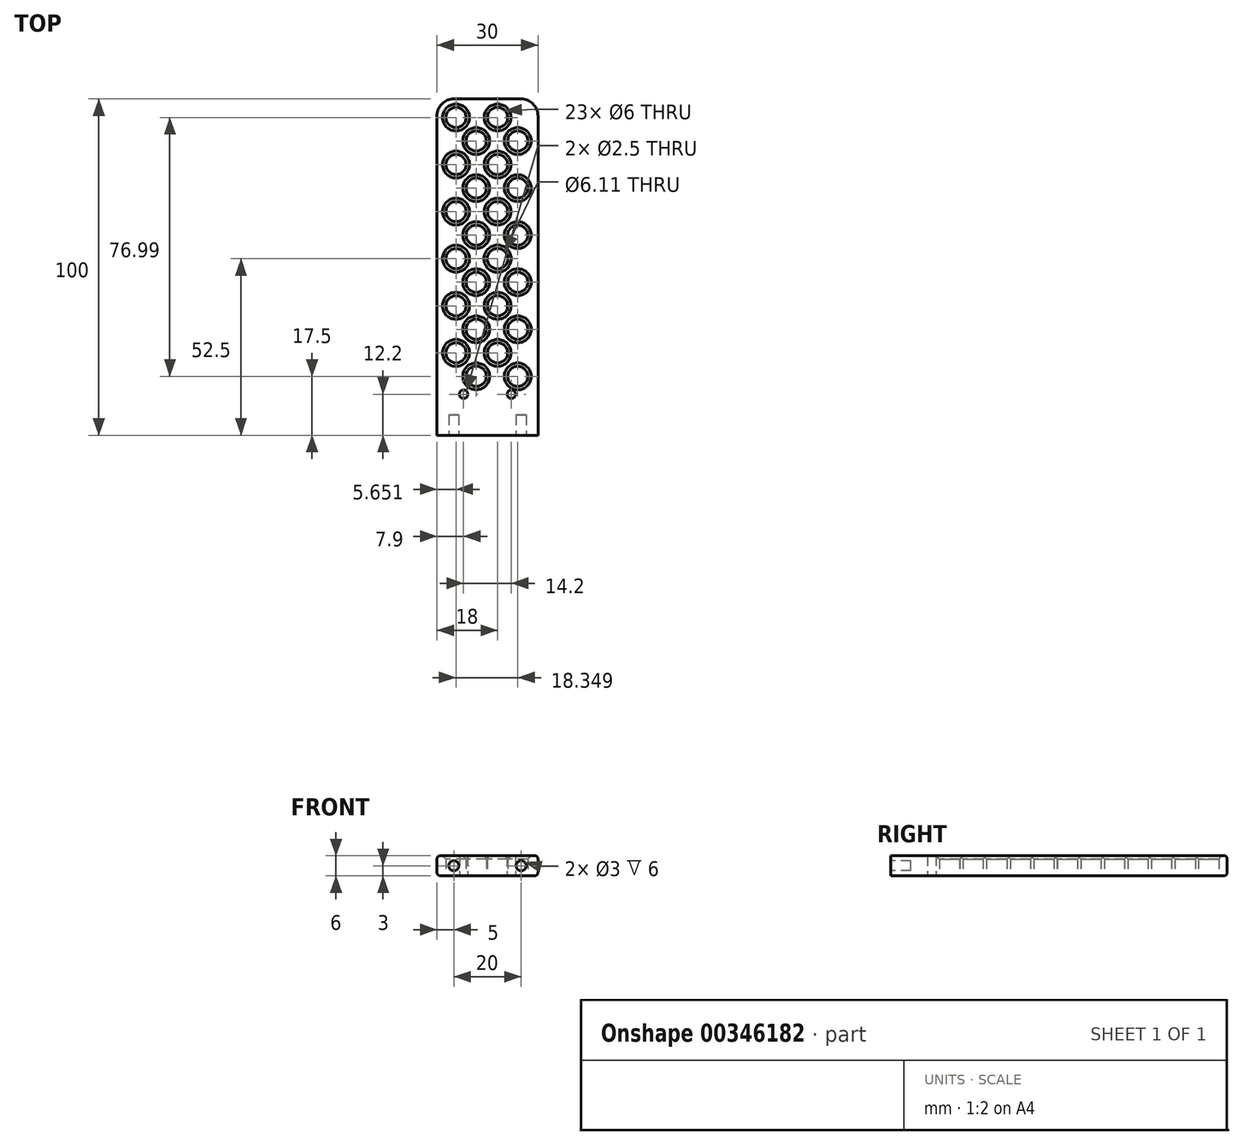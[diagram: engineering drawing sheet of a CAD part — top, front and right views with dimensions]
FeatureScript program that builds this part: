
annotation { "Feature Type Name" : "Feature", "Feature Type Description" : "" }
export const myFeature = defineFeature(function(context is Context, id is Id, definition is map)
    precondition{}
    {
        {
            var Q0;
            Q0=qCreatedBy(makeId("Top.planeOp"),FACE);
            var sketch = newSketch(context, id + "F0", { "sketchPlane" : qUnion([Q0])});
            skLineSegment(sketch, "E0.bottom", {"start": v(15, -50) * mm, "end": v(-15, -50) * mm});
            skLineSegment(sketch, "E0.top", {"start": v(15, 50) * mm, "end": v(-15, 50) * mm});
            skLineSegment(sketch, "E0.left", {"start": v(15, -50) * mm, "end": v(15, 50) * mm});
            skLineSegment(sketch, "E0.right", {"start": v(-15, -50) * mm, "end": v(-15, 50) * mm});
            skPoint(sketch, "E0.middle", {"position": v(0, 0) * mm});
            skLineSegment(sketch, "E1.bottom", {"start": v(-10, -27) * mm, "end": v(10, -27) * mm, "construction": true});
            skLineSegment(sketch, "E1.top", {"start": v(-10, -45) * mm, "end": v(10, -45) * mm, "construction": true});
            skLineSegment(sketch, "E1.left", {"start": v(-10, -27) * mm, "end": v(-10, -45) * mm, "construction": true});
            skLineSegment(sketch, "E1.right", {"start": v(10, -27) * mm, "end": v(10, -45) * mm, "construction": true});
            skCircle(sketch, "E2", {"center": v(-7.1, -37.8) * mm, "radius": 1.25 * mm});
            skCircle(sketch, "E3", {"center": v(7.1, -37.8) * mm, "radius": 1.25 * mm});
            skSolve(sketch);
        }
        {
            var Q0;
            Q0=makeQuery(id+"F0.imprint","IMPRINT",FACE,{"disambiguationData":[TD([[makeQuery(id+"F0.imprint","IMPRINT",EDGE,{"derivedFrom":sQuery(id+"F0.wireOp",EDGE,"E0.bottom")}),-1.0]])]});
            extrude(context, id + "F1", {"entities" : qUnion([Q0]), "depth" : 6 * mm});
        }
        {
            var Q0;
            Q0=qCreatedBy(makeId("Top.planeOp"),FACE);
            var sketch = newSketch(context, id + "F2", { "sketchPlane" : qUnion([Q0])});
            skLineSegment(sketch, "E4.bottom", {"start": v(-10, 45) * mm, "end": v(10, 45) * mm, "construction": true});
            skLineSegment(sketch, "E4.top", {"start": v(-10, -5) * mm, "end": v(10, -5) * mm, "construction": true});
            skLineSegment(sketch, "E4.left", {"start": v(-10, 45) * mm, "end": v(-10, -5) * mm, "construction": true});
            skLineSegment(sketch, "E4.right", {"start": v(10, 45) * mm, "end": v(10, -5) * mm, "construction": true});
            skPoint(sketch, "E4.middle", {"position": v(0, 20) * mm});
            skLineSegment(sketch, "E5", {"start": v(-3.35, -32.47) * mm, "end": v(-3.35, 45) * mm, "construction": true});
            skLineSegment(sketch, "E6", {"start": v(3, -32.47) * mm, "end": v(3, 45) * mm, "construction": true});
            skLineSegment(sketch, "E7", {"start": v(-15.35, -32.5) * mm, "end": v(15.58, -32.5) * mm, "construction": true});
            skLineSegment(sketch, "E8", {"start": v(9, -32.5) * mm, "end": v(9, 45) * mm, "construction": true});
            skLineSegment(sketch, "E9", {"start": v(-9.35, -32.5) * mm, "end": v(-9.35, 45) * mm, "construction": true});
            skLineSegment(sketch, "E10", {"start": v(-15.19, -25.5) * mm, "end": v(14.97, -25.5) * mm, "construction": true});
            skLineSegment(sketch, "E11", {"start": v(-15.19, -18.5) * mm, "end": v(15.13, -18.5) * mm, "construction": true});
            skLineSegment(sketch, "E12", {"start": v(-15.19, -11.5) * mm, "end": v(15.13, -11.5) * mm, "construction": true});
            skLineSegment(sketch, "E13", {"start": v(-15.19, -4.5) * mm, "end": v(15.13, -4.5) * mm, "construction": true});
            skCircle(sketch, "E14", {"center": v(-9.35, -25.5) * mm, "radius": 3 * mm});
            skCircle(sketch, "E15", {"center": v(-3.35, -18.5) * mm, "radius": 3 * mm});
            skCircle(sketch, "E16", {"center": v(3, -25.5) * mm, "radius": 3 * mm});
            skCircle(sketch, "E17", {"center": v(9, -18.5) * mm, "radius": 3 * mm});
            skCircle(sketch, "E18", {"center": v(9, -32.5) * mm, "radius": 3 * mm});
            skCircle(sketch, "E19", {"center": v(-3.35, -32.47) * mm, "radius": 3 * mm});
            skCircle(sketch, "E20", {"center": v(-9.35, -11.5) * mm, "radius": 3 * mm});
            skCircle(sketch, "E21", {"center": v(3, -11.5) * mm, "radius": 3 * mm});
            skLineSegment(sketch, "E22", {"start": v(-15.02, 2.5) * mm, "end": v(15.3, 2.5) * mm, "construction": true});
            skLineSegment(sketch, "E23", {"start": v(-15.17, 9.5) * mm, "end": v(15.3, 9.5) * mm, "construction": true});
            skLineSegment(sketch, "E24", {"start": v(-15.19, 16.5) * mm, "end": v(15.3, 16.5) * mm, "construction": true});
            skLineSegment(sketch, "E25", {"start": v(-15.02, 23.5) * mm, "end": v(15.3, 23.5) * mm, "construction": true});
            skLineSegment(sketch, "E26", {"start": v(-14.85, 30.5) * mm, "end": v(15.3, 30.5) * mm, "construction": true});
            skLineSegment(sketch, "E27", {"start": v(-14.85, 37.5) * mm, "end": v(15.3, 37.5) * mm, "construction": true});
            skLineSegment(sketch, "E28", {"start": v(-15.2, 44.49) * mm, "end": v(14.95, 44.49) * mm, "construction": true});
            skCircle(sketch, "E29", {"center": v(-3.35, -4.5) * mm, "radius": 3 * mm});
            skCircle(sketch, "E30", {"center": v(3, 2.5) * mm, "radius": 3.05 * mm});
            skCircle(sketch, "E31", {"center": v(9, 9.5) * mm, "radius": 3 * mm});
            skCircle(sketch, "E32", {"center": v(-3.35, 9.5) * mm, "radius": 3 * mm});
            skCircle(sketch, "E33", {"center": v(-9.35, 16.5) * mm, "radius": 3 * mm});
            skCircle(sketch, "E34", {"center": v(3, 16.5) * mm, "radius": 3 * mm});
            skCircle(sketch, "E35", {"center": v(-3.35, 23.5) * mm, "radius": 3 * mm});
            skCircle(sketch, "E36", {"center": v(-9.35, 30.5) * mm, "radius": 3 * mm});
            skCircle(sketch, "E37", {"center": v(3, 30.5) * mm, "radius": 3 * mm});
            skCircle(sketch, "E38", {"center": v(-3.35, 37.5) * mm, "radius": 3 * mm});
            skCircle(sketch, "E39", {"center": v(-9.35, 44.49) * mm, "radius": 3 * mm});
            skCircle(sketch, "E40", {"center": v(3, 44.49) * mm, "radius": 3 * mm});
            skCircle(sketch, "E41", {"center": v(9, -4.5) * mm, "radius": 3 * mm});
            skCircle(sketch, "E42", {"center": v(9, 23.5) * mm, "radius": 3 * mm});
            skCircle(sketch, "E43", {"center": v(9, 37.5) * mm, "radius": 3 * mm});
            skCircle(sketch, "E44", {"center": v(-9.35, 2.5) * mm, "radius": 3 * mm});
            skSolve(sketch);
        }
        {
            var Q0;
            Q0 = qSketchRegion(id + "F2", true);
            extrude(context, id + "F3", {"entities" : qUnion([Q0]), "operationType" : NewBodyOperationType.REMOVE, "endBound" : BoundingType.THROUGH_ALL, "depth" : 25 * mm});
        }
        {
            var Q0;
            Q0=makeQuery(id+"F1.opExtrude","SWEPT_EDGE",EDGE,{"disambiguationData":[OSD([sQuery(id+"F0.wireOp",EDGE,"E0.top"),sQuery(id+"F0.wireOp",EDGE,"E0.left")])]});
            var Q1;
            Q1=makeQuery(id+"F1.opExtrude","SWEPT_EDGE",EDGE,{"disambiguationData":[OSD([sQuery(id+"F0.wireOp",EDGE,"E0.top"),sQuery(id+"F0.wireOp",EDGE,"E0.right")])]});
            fillet(context, id + "F4", {"entities" : qUnion([Q0, Q1]), "radius" : 5 * mm, "tangentPropagation" : true, "allowEdgeOverflow" : false});
        }
        {
            var Q0;
            Q0=makeQuery(id+"F3.boolean.opBoolean","INTERSECT",EDGE,{"derivedFrom":[makeQuery(id+"F1.opExtrude","CAP_FACE",FACE,{"disambiguationData":[OSD([sQuery(id+"F0.wireOp",EDGE,"E0.bottom"),sQuery(id+"F0.wireOp",EDGE,"E0.top"),sQuery(id+"F0.wireOp",EDGE,"E0.left"),sQuery(id+"F0.wireOp",EDGE,"E0.right"),sQuery(id+"F0.wireOp",EDGE,"E2"),sQuery(id+"F0.wireOp",EDGE,"E3")])],"isStart":false}),makeQuery(id+"F3.opExtrude","SWEPT_FACE",FACE,{"disambiguationData":[OSD([sQuery(id+"F2.wireOp",EDGE,"E19")])]})]});
            var Q1;
            Q1=makeQuery(id+"F3.boolean.opBoolean","INTERSECT",EDGE,{"derivedFrom":[makeQuery(id+"F1.opExtrude","CAP_FACE",FACE,{"disambiguationData":[OSD([sQuery(id+"F0.wireOp",EDGE,"E0.bottom"),sQuery(id+"F0.wireOp",EDGE,"E0.top"),sQuery(id+"F0.wireOp",EDGE,"E0.left"),sQuery(id+"F0.wireOp",EDGE,"E0.right"),sQuery(id+"F0.wireOp",EDGE,"E2"),sQuery(id+"F0.wireOp",EDGE,"E3")])],"isStart":false}),makeQuery(id+"F3.opExtrude","SWEPT_FACE",FACE,{"disambiguationData":[OSD([sQuery(id+"F2.wireOp",EDGE,"E14")])]})]});
            var Q2;
            Q2=makeQuery(id+"F3.boolean.opBoolean","INTERSECT",EDGE,{"derivedFrom":[makeQuery(id+"F1.opExtrude","CAP_FACE",FACE,{"disambiguationData":[OSD([sQuery(id+"F0.wireOp",EDGE,"E0.bottom"),sQuery(id+"F0.wireOp",EDGE,"E0.top"),sQuery(id+"F0.wireOp",EDGE,"E0.left"),sQuery(id+"F0.wireOp",EDGE,"E0.right"),sQuery(id+"F0.wireOp",EDGE,"E2"),sQuery(id+"F0.wireOp",EDGE,"E3")])],"isStart":false}),makeQuery(id+"F3.opExtrude","SWEPT_FACE",FACE,{"disambiguationData":[OSD([sQuery(id+"F2.wireOp",EDGE,"E15")])]})]});
            var Q3;
            Q3=makeQuery(id+"F3.boolean.opBoolean","INTERSECT",EDGE,{"derivedFrom":[makeQuery(id+"F1.opExtrude","CAP_FACE",FACE,{"disambiguationData":[OSD([sQuery(id+"F0.wireOp",EDGE,"E0.bottom"),sQuery(id+"F0.wireOp",EDGE,"E0.top"),sQuery(id+"F0.wireOp",EDGE,"E0.left"),sQuery(id+"F0.wireOp",EDGE,"E0.right"),sQuery(id+"F0.wireOp",EDGE,"E2"),sQuery(id+"F0.wireOp",EDGE,"E3")])],"isStart":false}),makeQuery(id+"F3.opExtrude","SWEPT_FACE",FACE,{"disambiguationData":[OSD([sQuery(id+"F2.wireOp",EDGE,"E16")])]})]});
            var Q4;
            Q4=makeQuery(id+"F3.boolean.opBoolean","INTERSECT",EDGE,{"derivedFrom":[makeQuery(id+"F1.opExtrude","CAP_FACE",FACE,{"disambiguationData":[OSD([sQuery(id+"F0.wireOp",EDGE,"E0.bottom"),sQuery(id+"F0.wireOp",EDGE,"E0.top"),sQuery(id+"F0.wireOp",EDGE,"E0.left"),sQuery(id+"F0.wireOp",EDGE,"E0.right"),sQuery(id+"F0.wireOp",EDGE,"E2"),sQuery(id+"F0.wireOp",EDGE,"E3")])],"isStart":false}),makeQuery(id+"F3.opExtrude","SWEPT_FACE",FACE,{"disambiguationData":[OSD([sQuery(id+"F2.wireOp",EDGE,"E18")])]})]});
            var Q5;
            Q5=makeQuery(id+"F3.boolean.opBoolean","INTERSECT",EDGE,{"derivedFrom":[makeQuery(id+"F1.opExtrude","CAP_FACE",FACE,{"disambiguationData":[OSD([sQuery(id+"F0.wireOp",EDGE,"E0.bottom"),sQuery(id+"F0.wireOp",EDGE,"E0.top"),sQuery(id+"F0.wireOp",EDGE,"E0.left"),sQuery(id+"F0.wireOp",EDGE,"E0.right"),sQuery(id+"F0.wireOp",EDGE,"E2"),sQuery(id+"F0.wireOp",EDGE,"E3")])],"isStart":false}),makeQuery(id+"F3.opExtrude","SWEPT_FACE",FACE,{"disambiguationData":[OSD([sQuery(id+"F2.wireOp",EDGE,"E17")])]})]});
            var Q6;
            Q6=makeQuery(id+"F3.boolean.opBoolean","INTERSECT",EDGE,{"derivedFrom":[makeQuery(id+"F1.opExtrude","CAP_FACE",FACE,{"disambiguationData":[OSD([sQuery(id+"F0.wireOp",EDGE,"E0.bottom"),sQuery(id+"F0.wireOp",EDGE,"E0.top"),sQuery(id+"F0.wireOp",EDGE,"E0.left"),sQuery(id+"F0.wireOp",EDGE,"E0.right"),sQuery(id+"F0.wireOp",EDGE,"E2"),sQuery(id+"F0.wireOp",EDGE,"E3")])],"isStart":false}),makeQuery(id+"F3.opExtrude","SWEPT_FACE",FACE,{"disambiguationData":[OSD([sQuery(id+"F2.wireOp",EDGE,"E21")])]})]});
            var Q7;
            Q7=makeQuery(id+"F3.boolean.opBoolean","INTERSECT",EDGE,{"derivedFrom":[makeQuery(id+"F1.opExtrude","CAP_FACE",FACE,{"disambiguationData":[OSD([sQuery(id+"F0.wireOp",EDGE,"E0.bottom"),sQuery(id+"F0.wireOp",EDGE,"E0.top"),sQuery(id+"F0.wireOp",EDGE,"E0.left"),sQuery(id+"F0.wireOp",EDGE,"E0.right"),sQuery(id+"F0.wireOp",EDGE,"E2"),sQuery(id+"F0.wireOp",EDGE,"E3")])],"isStart":false}),makeQuery(id+"F3.opExtrude","SWEPT_FACE",FACE,{"disambiguationData":[OSD([sQuery(id+"F2.wireOp",EDGE,"E20")])]})]});
            var Q8;
            Q8=makeQuery(id+"F3.boolean.opBoolean","INTERSECT",EDGE,{"derivedFrom":[makeQuery(id+"F1.opExtrude","CAP_FACE",FACE,{"disambiguationData":[OSD([sQuery(id+"F0.wireOp",EDGE,"E0.bottom"),sQuery(id+"F0.wireOp",EDGE,"E0.top"),sQuery(id+"F0.wireOp",EDGE,"E0.left"),sQuery(id+"F0.wireOp",EDGE,"E0.right"),sQuery(id+"F0.wireOp",EDGE,"E2"),sQuery(id+"F0.wireOp",EDGE,"E3")])],"isStart":false}),makeQuery(id+"F3.opExtrude","SWEPT_FACE",FACE,{"disambiguationData":[OSD([sQuery(id+"F2.wireOp",EDGE,"E29")])]})]});
            var Q9;
            Q9=makeQuery(id+"F3.boolean.opBoolean","INTERSECT",EDGE,{"derivedFrom":[makeQuery(id+"F1.opExtrude","CAP_FACE",FACE,{"disambiguationData":[OSD([sQuery(id+"F0.wireOp",EDGE,"E0.bottom"),sQuery(id+"F0.wireOp",EDGE,"E0.top"),sQuery(id+"F0.wireOp",EDGE,"E0.left"),sQuery(id+"F0.wireOp",EDGE,"E0.right"),sQuery(id+"F0.wireOp",EDGE,"E2"),sQuery(id+"F0.wireOp",EDGE,"E3")])],"isStart":false}),makeQuery(id+"F3.opExtrude","SWEPT_FACE",FACE,{"disambiguationData":[OSD([sQuery(id+"F2.wireOp",EDGE,"E44")])]})]});
            var Q10;
            Q10=makeQuery(id+"F3.boolean.opBoolean","INTERSECT",EDGE,{"derivedFrom":[makeQuery(id+"F1.opExtrude","CAP_FACE",FACE,{"disambiguationData":[OSD([sQuery(id+"F0.wireOp",EDGE,"E0.bottom"),sQuery(id+"F0.wireOp",EDGE,"E0.top"),sQuery(id+"F0.wireOp",EDGE,"E0.left"),sQuery(id+"F0.wireOp",EDGE,"E0.right"),sQuery(id+"F0.wireOp",EDGE,"E2"),sQuery(id+"F0.wireOp",EDGE,"E3")])],"isStart":false}),makeQuery(id+"F3.opExtrude","SWEPT_FACE",FACE,{"disambiguationData":[OSD([sQuery(id+"F2.wireOp",EDGE,"E30")])]})]});
            var Q11;
            Q11=makeQuery(id+"F3.boolean.opBoolean","INTERSECT",EDGE,{"derivedFrom":[makeQuery(id+"F1.opExtrude","CAP_FACE",FACE,{"disambiguationData":[OSD([sQuery(id+"F0.wireOp",EDGE,"E0.bottom"),sQuery(id+"F0.wireOp",EDGE,"E0.top"),sQuery(id+"F0.wireOp",EDGE,"E0.left"),sQuery(id+"F0.wireOp",EDGE,"E0.right"),sQuery(id+"F0.wireOp",EDGE,"E2"),sQuery(id+"F0.wireOp",EDGE,"E3")])],"isStart":false}),makeQuery(id+"F3.opExtrude","SWEPT_FACE",FACE,{"disambiguationData":[OSD([sQuery(id+"F2.wireOp",EDGE,"E41")])]})]});
            var Q12;
            Q12=makeQuery(id+"F3.boolean.opBoolean","INTERSECT",EDGE,{"derivedFrom":[makeQuery(id+"F1.opExtrude","CAP_FACE",FACE,{"disambiguationData":[OSD([sQuery(id+"F0.wireOp",EDGE,"E0.bottom"),sQuery(id+"F0.wireOp",EDGE,"E0.top"),sQuery(id+"F0.wireOp",EDGE,"E0.left"),sQuery(id+"F0.wireOp",EDGE,"E0.right"),sQuery(id+"F0.wireOp",EDGE,"E2"),sQuery(id+"F0.wireOp",EDGE,"E3")])],"isStart":false}),makeQuery(id+"F3.opExtrude","SWEPT_FACE",FACE,{"disambiguationData":[OSD([sQuery(id+"F2.wireOp",EDGE,"E31")])]})]});
            var Q13;
            Q13=makeQuery(id+"F3.boolean.opBoolean","INTERSECT",EDGE,{"derivedFrom":[makeQuery(id+"F1.opExtrude","CAP_FACE",FACE,{"disambiguationData":[OSD([sQuery(id+"F0.wireOp",EDGE,"E0.bottom"),sQuery(id+"F0.wireOp",EDGE,"E0.top"),sQuery(id+"F0.wireOp",EDGE,"E0.left"),sQuery(id+"F0.wireOp",EDGE,"E0.right"),sQuery(id+"F0.wireOp",EDGE,"E2"),sQuery(id+"F0.wireOp",EDGE,"E3")])],"isStart":false}),makeQuery(id+"F3.opExtrude","SWEPT_FACE",FACE,{"disambiguationData":[OSD([sQuery(id+"F2.wireOp",EDGE,"E32")])]})]});
            var Q14;
            Q14=makeQuery(id+"F3.boolean.opBoolean","INTERSECT",EDGE,{"derivedFrom":[makeQuery(id+"F1.opExtrude","CAP_FACE",FACE,{"disambiguationData":[OSD([sQuery(id+"F0.wireOp",EDGE,"E0.bottom"),sQuery(id+"F0.wireOp",EDGE,"E0.top"),sQuery(id+"F0.wireOp",EDGE,"E0.left"),sQuery(id+"F0.wireOp",EDGE,"E0.right"),sQuery(id+"F0.wireOp",EDGE,"E2"),sQuery(id+"F0.wireOp",EDGE,"E3")])],"isStart":false}),makeQuery(id+"F3.opExtrude","SWEPT_FACE",FACE,{"disambiguationData":[OSD([sQuery(id+"F2.wireOp",EDGE,"E33")])]})]});
            var Q15;
            Q15=makeQuery(id+"F3.boolean.opBoolean","INTERSECT",EDGE,{"derivedFrom":[makeQuery(id+"F1.opExtrude","CAP_FACE",FACE,{"disambiguationData":[OSD([sQuery(id+"F0.wireOp",EDGE,"E0.bottom"),sQuery(id+"F0.wireOp",EDGE,"E0.top"),sQuery(id+"F0.wireOp",EDGE,"E0.left"),sQuery(id+"F0.wireOp",EDGE,"E0.right"),sQuery(id+"F0.wireOp",EDGE,"E2"),sQuery(id+"F0.wireOp",EDGE,"E3")])],"isStart":false}),makeQuery(id+"F3.opExtrude","SWEPT_FACE",FACE,{"disambiguationData":[OSD([sQuery(id+"F2.wireOp",EDGE,"E35")])]})]});
            var Q16;
            Q16=makeQuery(id+"F3.boolean.opBoolean","INTERSECT",EDGE,{"derivedFrom":[makeQuery(id+"F1.opExtrude","CAP_FACE",FACE,{"disambiguationData":[OSD([sQuery(id+"F0.wireOp",EDGE,"E0.bottom"),sQuery(id+"F0.wireOp",EDGE,"E0.top"),sQuery(id+"F0.wireOp",EDGE,"E0.left"),sQuery(id+"F0.wireOp",EDGE,"E0.right"),sQuery(id+"F0.wireOp",EDGE,"E2"),sQuery(id+"F0.wireOp",EDGE,"E3")])],"isStart":false}),makeQuery(id+"F3.opExtrude","SWEPT_FACE",FACE,{"disambiguationData":[OSD([sQuery(id+"F2.wireOp",EDGE,"E34")])]})]});
            var Q17;
            Q17=makeQuery(id+"F3.boolean.opBoolean","INTERSECT",EDGE,{"derivedFrom":[makeQuery(id+"F1.opExtrude","CAP_FACE",FACE,{"disambiguationData":[OSD([sQuery(id+"F0.wireOp",EDGE,"E0.bottom"),sQuery(id+"F0.wireOp",EDGE,"E0.top"),sQuery(id+"F0.wireOp",EDGE,"E0.left"),sQuery(id+"F0.wireOp",EDGE,"E0.right"),sQuery(id+"F0.wireOp",EDGE,"E2"),sQuery(id+"F0.wireOp",EDGE,"E3")])],"isStart":false}),makeQuery(id+"F3.opExtrude","SWEPT_FACE",FACE,{"disambiguationData":[OSD([sQuery(id+"F2.wireOp",EDGE,"E42")])]})]});
            var Q18;
            Q18=makeQuery(id+"F3.boolean.opBoolean","INTERSECT",EDGE,{"derivedFrom":[makeQuery(id+"F1.opExtrude","CAP_FACE",FACE,{"disambiguationData":[OSD([sQuery(id+"F0.wireOp",EDGE,"E0.bottom"),sQuery(id+"F0.wireOp",EDGE,"E0.top"),sQuery(id+"F0.wireOp",EDGE,"E0.left"),sQuery(id+"F0.wireOp",EDGE,"E0.right"),sQuery(id+"F0.wireOp",EDGE,"E2"),sQuery(id+"F0.wireOp",EDGE,"E3")])],"isStart":false}),makeQuery(id+"F3.opExtrude","SWEPT_FACE",FACE,{"disambiguationData":[OSD([sQuery(id+"F2.wireOp",EDGE,"E37")])]})]});
            var Q19;
            Q19=makeQuery(id+"F3.boolean.opBoolean","INTERSECT",EDGE,{"derivedFrom":[makeQuery(id+"F1.opExtrude","CAP_FACE",FACE,{"disambiguationData":[OSD([sQuery(id+"F0.wireOp",EDGE,"E0.bottom"),sQuery(id+"F0.wireOp",EDGE,"E0.top"),sQuery(id+"F0.wireOp",EDGE,"E0.left"),sQuery(id+"F0.wireOp",EDGE,"E0.right"),sQuery(id+"F0.wireOp",EDGE,"E2"),sQuery(id+"F0.wireOp",EDGE,"E3")])],"isStart":false}),makeQuery(id+"F3.opExtrude","SWEPT_FACE",FACE,{"disambiguationData":[OSD([sQuery(id+"F2.wireOp",EDGE,"E43")])]})]});
            var Q20;
            Q20=makeQuery(id+"F3.boolean.opBoolean","INTERSECT",EDGE,{"derivedFrom":[makeQuery(id+"F1.opExtrude","CAP_FACE",FACE,{"disambiguationData":[OSD([sQuery(id+"F0.wireOp",EDGE,"E0.bottom"),sQuery(id+"F0.wireOp",EDGE,"E0.top"),sQuery(id+"F0.wireOp",EDGE,"E0.left"),sQuery(id+"F0.wireOp",EDGE,"E0.right"),sQuery(id+"F0.wireOp",EDGE,"E2"),sQuery(id+"F0.wireOp",EDGE,"E3")])],"isStart":false}),makeQuery(id+"F3.opExtrude","SWEPT_FACE",FACE,{"disambiguationData":[OSD([sQuery(id+"F2.wireOp",EDGE,"E40")])]})]});
            var Q21;
            Q21=makeQuery(id+"F3.boolean.opBoolean","INTERSECT",EDGE,{"derivedFrom":[makeQuery(id+"F1.opExtrude","CAP_FACE",FACE,{"disambiguationData":[OSD([sQuery(id+"F0.wireOp",EDGE,"E0.bottom"),sQuery(id+"F0.wireOp",EDGE,"E0.top"),sQuery(id+"F0.wireOp",EDGE,"E0.left"),sQuery(id+"F0.wireOp",EDGE,"E0.right"),sQuery(id+"F0.wireOp",EDGE,"E2"),sQuery(id+"F0.wireOp",EDGE,"E3")])],"isStart":false}),makeQuery(id+"F3.opExtrude","SWEPT_FACE",FACE,{"disambiguationData":[OSD([sQuery(id+"F2.wireOp",EDGE,"E38")])]})]});
            var Q22;
            Q22=makeQuery(id+"F3.boolean.opBoolean","INTERSECT",EDGE,{"derivedFrom":[makeQuery(id+"F1.opExtrude","CAP_FACE",FACE,{"disambiguationData":[OSD([sQuery(id+"F0.wireOp",EDGE,"E0.bottom"),sQuery(id+"F0.wireOp",EDGE,"E0.top"),sQuery(id+"F0.wireOp",EDGE,"E0.left"),sQuery(id+"F0.wireOp",EDGE,"E0.right"),sQuery(id+"F0.wireOp",EDGE,"E2"),sQuery(id+"F0.wireOp",EDGE,"E3")])],"isStart":false}),makeQuery(id+"F3.opExtrude","SWEPT_FACE",FACE,{"disambiguationData":[OSD([sQuery(id+"F2.wireOp",EDGE,"E39")])]})]});
            var Q23;
            Q23=makeQuery(id+"F3.boolean.opBoolean","INTERSECT",EDGE,{"derivedFrom":[makeQuery(id+"F1.opExtrude","CAP_FACE",FACE,{"disambiguationData":[OSD([sQuery(id+"F0.wireOp",EDGE,"E0.bottom"),sQuery(id+"F0.wireOp",EDGE,"E0.top"),sQuery(id+"F0.wireOp",EDGE,"E0.left"),sQuery(id+"F0.wireOp",EDGE,"E0.right"),sQuery(id+"F0.wireOp",EDGE,"E2"),sQuery(id+"F0.wireOp",EDGE,"E3")])],"isStart":false}),makeQuery(id+"F3.opExtrude","SWEPT_FACE",FACE,{"disambiguationData":[OSD([sQuery(id+"F2.wireOp",EDGE,"E36")])]})]});
            var Q24;
            Q24=makeQuery(id+"F3.boolean.opBoolean","COPY",EDGE,{"derivedFrom":makeQuery(id+"F3.opExtrude","CAP_EDGE",EDGE,{"disambiguationData":[OSD([sQuery(id+"F2.wireOp",EDGE,"E18")])],"isStart":true})});
            var Q25;
            Q25=makeQuery(id+"F3.boolean.opBoolean","COPY",EDGE,{"derivedFrom":makeQuery(id+"F3.opExtrude","CAP_EDGE",EDGE,{"disambiguationData":[OSD([sQuery(id+"F2.wireOp",EDGE,"E19")])],"isStart":true})});
            var Q26;
            Q26=makeQuery(id+"F3.boolean.opBoolean","COPY",EDGE,{"derivedFrom":makeQuery(id+"F3.opExtrude","CAP_EDGE",EDGE,{"disambiguationData":[OSD([sQuery(id+"F2.wireOp",EDGE,"E14")])],"isStart":true})});
            var Q27;
            Q27=makeQuery(id+"F3.boolean.opBoolean","COPY",EDGE,{"derivedFrom":makeQuery(id+"F3.opExtrude","CAP_EDGE",EDGE,{"disambiguationData":[OSD([sQuery(id+"F2.wireOp",EDGE,"E16")])],"isStart":true})});
            var Q28;
            Q28=makeQuery(id+"F3.boolean.opBoolean","COPY",EDGE,{"derivedFrom":makeQuery(id+"F3.opExtrude","CAP_EDGE",EDGE,{"disambiguationData":[OSD([sQuery(id+"F2.wireOp",EDGE,"E17")])],"isStart":true})});
            var Q29;
            Q29=makeQuery(id+"F3.boolean.opBoolean","COPY",EDGE,{"derivedFrom":makeQuery(id+"F3.opExtrude","CAP_EDGE",EDGE,{"disambiguationData":[OSD([sQuery(id+"F2.wireOp",EDGE,"E15")])],"isStart":true})});
            var Q30;
            Q30=makeQuery(id+"F3.boolean.opBoolean","COPY",EDGE,{"derivedFrom":makeQuery(id+"F3.opExtrude","CAP_EDGE",EDGE,{"disambiguationData":[OSD([sQuery(id+"F2.wireOp",EDGE,"E20")])],"isStart":true})});
            var Q31;
            Q31=makeQuery(id+"F3.boolean.opBoolean","COPY",EDGE,{"derivedFrom":makeQuery(id+"F3.opExtrude","CAP_EDGE",EDGE,{"disambiguationData":[OSD([sQuery(id+"F2.wireOp",EDGE,"E21")])],"isStart":true})});
            var Q32;
            Q32=makeQuery(id+"F3.boolean.opBoolean","COPY",EDGE,{"derivedFrom":makeQuery(id+"F3.opExtrude","CAP_EDGE",EDGE,{"disambiguationData":[OSD([sQuery(id+"F2.wireOp",EDGE,"E41")])],"isStart":true})});
            var Q33;
            Q33=makeQuery(id+"F3.boolean.opBoolean","COPY",EDGE,{"derivedFrom":makeQuery(id+"F3.opExtrude","CAP_EDGE",EDGE,{"disambiguationData":[OSD([sQuery(id+"F2.wireOp",EDGE,"E29")])],"isStart":true})});
            var Q34;
            Q34=makeQuery(id+"F3.boolean.opBoolean","COPY",EDGE,{"derivedFrom":makeQuery(id+"F3.opExtrude","CAP_EDGE",EDGE,{"disambiguationData":[OSD([sQuery(id+"F2.wireOp",EDGE,"E30")])],"isStart":true})});
            var Q35;
            Q35=makeQuery(id+"F3.boolean.opBoolean","COPY",EDGE,{"derivedFrom":makeQuery(id+"F3.opExtrude","CAP_EDGE",EDGE,{"disambiguationData":[OSD([sQuery(id+"F2.wireOp",EDGE,"E44")])],"isStart":true})});
            var Q36;
            Q36=makeQuery(id+"F3.boolean.opBoolean","COPY",EDGE,{"derivedFrom":makeQuery(id+"F3.opExtrude","CAP_EDGE",EDGE,{"disambiguationData":[OSD([sQuery(id+"F2.wireOp",EDGE,"E32")])],"isStart":true})});
            var Q37;
            Q37=makeQuery(id+"F3.boolean.opBoolean","COPY",EDGE,{"derivedFrom":makeQuery(id+"F3.opExtrude","CAP_EDGE",EDGE,{"disambiguationData":[OSD([sQuery(id+"F2.wireOp",EDGE,"E31")])],"isStart":true})});
            var Q38;
            Q38=makeQuery(id+"F3.boolean.opBoolean","COPY",EDGE,{"derivedFrom":makeQuery(id+"F3.opExtrude","CAP_EDGE",EDGE,{"disambiguationData":[OSD([sQuery(id+"F2.wireOp",EDGE,"E34")])],"isStart":true})});
            var Q39;
            Q39=makeQuery(id+"F3.boolean.opBoolean","COPY",EDGE,{"derivedFrom":makeQuery(id+"F3.opExtrude","CAP_EDGE",EDGE,{"disambiguationData":[OSD([sQuery(id+"F2.wireOp",EDGE,"E33")])],"isStart":true})});
            var Q40;
            Q40=makeQuery(id+"F3.boolean.opBoolean","COPY",EDGE,{"derivedFrom":makeQuery(id+"F3.opExtrude","CAP_EDGE",EDGE,{"disambiguationData":[OSD([sQuery(id+"F2.wireOp",EDGE,"E42")])],"isStart":true})});
            var Q41;
            Q41=makeQuery(id+"F3.boolean.opBoolean","COPY",EDGE,{"derivedFrom":makeQuery(id+"F3.opExtrude","CAP_EDGE",EDGE,{"disambiguationData":[OSD([sQuery(id+"F2.wireOp",EDGE,"E35")])],"isStart":true})});
            var Q42;
            Q42=makeQuery(id+"F3.boolean.opBoolean","COPY",EDGE,{"derivedFrom":makeQuery(id+"F3.opExtrude","CAP_EDGE",EDGE,{"disambiguationData":[OSD([sQuery(id+"F2.wireOp",EDGE,"E36")])],"isStart":true})});
            var Q43;
            Q43=makeQuery(id+"F3.boolean.opBoolean","COPY",EDGE,{"derivedFrom":makeQuery(id+"F3.opExtrude","CAP_EDGE",EDGE,{"disambiguationData":[OSD([sQuery(id+"F2.wireOp",EDGE,"E37")])],"isStart":true})});
            var Q44;
            Q44=makeQuery(id+"F3.boolean.opBoolean","COPY",EDGE,{"derivedFrom":makeQuery(id+"F3.opExtrude","CAP_EDGE",EDGE,{"disambiguationData":[OSD([sQuery(id+"F2.wireOp",EDGE,"E43")])],"isStart":true})});
            var Q45;
            Q45=makeQuery(id+"F3.boolean.opBoolean","COPY",EDGE,{"derivedFrom":makeQuery(id+"F3.opExtrude","CAP_EDGE",EDGE,{"disambiguationData":[OSD([sQuery(id+"F2.wireOp",EDGE,"E38")])],"isStart":true})});
            var Q46;
            Q46=makeQuery(id+"F3.boolean.opBoolean","COPY",EDGE,{"derivedFrom":makeQuery(id+"F3.opExtrude","CAP_EDGE",EDGE,{"disambiguationData":[OSD([sQuery(id+"F2.wireOp",EDGE,"E40")])],"isStart":true})});
            var Q47;
            Q47=makeQuery(id+"F3.boolean.opBoolean","COPY",EDGE,{"derivedFrom":makeQuery(id+"F3.opExtrude","CAP_EDGE",EDGE,{"disambiguationData":[OSD([sQuery(id+"F2.wireOp",EDGE,"E39")])],"isStart":true})});
            chamfer(context, id + "F5", {"entities" : qUnion([Q0, Q1, Q2, Q3, Q4, Q5, Q6, Q7, Q8, Q9, Q10, Q11, Q12, Q13, Q14, Q15, Q16, Q17, Q18, Q19, Q20, Q21, Q22, Q23, Q24, Q25, Q26, Q27, Q28, Q29, Q30, Q31, Q32, Q33, Q34, Q35, Q36, Q37, Q38, Q39, Q40, Q41, Q42, Q43, Q44, Q45, Q46, Q47]), "width" : 1 * mm, "tangentPropagation" : true});
        }
        {
            var Q0;
            Q0=makeQuery(id+"F1.opExtrude","CAP_EDGE",EDGE,{"disambiguationData":[OSD([sQuery(id+"F0.wireOp",EDGE,"E0.left")])],"isStart":false});
            var Q1;
            Q1=makeQuery(id+"F1.opExtrude","CAP_EDGE",EDGE,{"disambiguationData":[OSD([sQuery(id+"F0.wireOp",EDGE,"E0.left")])],"isStart":true});
            var Q2;
            {var subQ0=sQuery(id+"F0.wireOp",EDGE,"E0.left");var subQ1=sQuery(id+"F0.wireOp",EDGE,"E0.top");Q2=makeQuery(id+"F4.opFillet","BLEND_EDGE",EDGE,{"blendedFrom":[makeQuery(id+"F1.opExtrude","SWEPT_EDGE",EDGE,{"disambiguationData":[OSD([subQ1,subQ0])]}),makeQuery(id+"F1.opExtrude","CAP_FACE",FACE,{"disambiguationData":[OSD([sQuery(id+"F0.wireOp",EDGE,"E0.bottom"),subQ1,subQ0,sQuery(id+"F0.wireOp",EDGE,"E0.right"),sQuery(id+"F0.wireOp",EDGE,"E2"),sQuery(id+"F0.wireOp",EDGE,"E3")])],"isStart":true})],"blendedInto":[makeQuery(id+"F1.opExtrude","CAP_FACE",FACE,{"disambiguationData":[OSD([sQuery(id+"F0.wireOp",EDGE,"E0.bottom"),subQ1,subQ0,sQuery(id+"F0.wireOp",EDGE,"E0.right"),sQuery(id+"F0.wireOp",EDGE,"E2"),sQuery(id+"F0.wireOp",EDGE,"E3")])],"isStart":true})]});}
            fillet(context, id + "F6", {"entities" : qUnion([Q0, Q1, Q2]), "radius" : 1 * mm, "tangentPropagation" : true, "allowEdgeOverflow" : false});
        }
        {
            var Q0;
            Q0=makeQuery(id+"F1.opExtrude","SWEPT_FACE",FACE,{"disambiguationData":[OSD([sQuery(id+"F0.wireOp",EDGE,"E0.bottom")])]});
            var sketch = newSketch(context, id + "F7", { "sketchPlane" : qUnion([Q0])});
            skCircle(sketch, "E45", {"center": v(-10, 3) * mm, "radius": 1.5 * mm});
            skPoint(sketch, "E45.centerSnap0", {"position": v(-15, 3) * mm});
            skCircle(sketch, "E46", {"center": v(10, 3) * mm, "radius": 1.5 * mm});
            skSolve(sketch);
        }
        {
            var Q0;
            Q0=makeQuery(id+"F7.imprint","IMPRINT",FACE,{"disambiguationData":[TD([[makeQuery(id+"F7.imprint","IMPRINT",EDGE,{"derivedFrom":sQuery(id+"F7.wireOp",EDGE,"E45")}),1.0]])]});
            var Q1;
            Q1=makeQuery(id+"F7.imprint","IMPRINT",FACE,{"disambiguationData":[TD([[makeQuery(id+"F7.imprint","IMPRINT",EDGE,{"derivedFrom":sQuery(id+"F7.wireOp",EDGE,"E46")}),1.0]])]});
            extrude(context, id + "F8", {"entities" : qUnion([Q0, Q1]), "operationType" : NewBodyOperationType.REMOVE, "oppositeDirection" : true, "depth" : 6 * mm});
        }
    });
